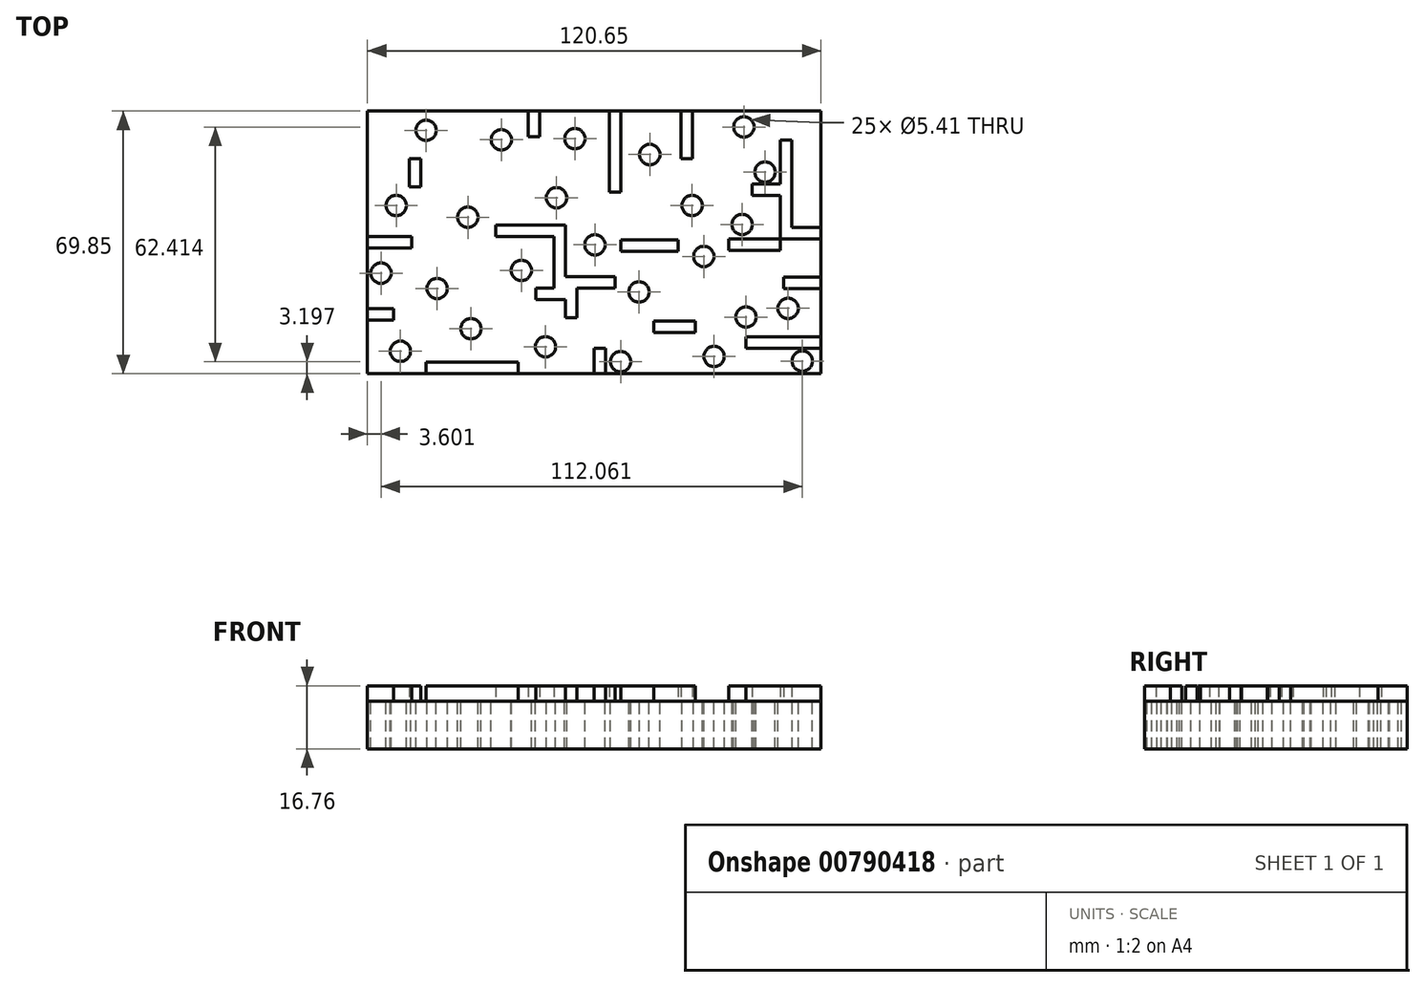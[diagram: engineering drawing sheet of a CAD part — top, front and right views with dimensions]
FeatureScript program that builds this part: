
annotation { "Feature Type Name" : "Feature", "Feature Type Description" : "" }
export const myFeature = defineFeature(function(context is Context, id is Id, definition is map)
    precondition{}
    {
        {
            var Q0;
            Q0=qCreatedBy(makeId("Top.planeOp"),FACE);
            var sketch = newSketch(context, id + "F0", { "sketchPlane" : qUnion([Q0])});
            skLineSegment(sketch, "E0.bottom", {"start": v(-60.33, 0) * mm, "end": v(60.33, 0) * mm});
            skLineSegment(sketch, "E0.top", {"start": v(-60.32, -69.85) * mm, "end": v(60.33, -69.85) * mm});
            skLineSegment(sketch, "E0.left", {"start": v(-60.33, 0) * mm, "end": v(-60.32, -69.85) * mm});
            skLineSegment(sketch, "E0.right", {"start": v(60.33, 0) * mm, "end": v(60.33, -69.85) * mm});
            skLineSegment(sketch, "E1", {"start": v(-60.33, 0) * mm, "end": v(0, 0) * mm});
            skLineSegment(sketch, "E2", {"start": v(0, 0) * mm, "end": v(60.33, 0) * mm});
            skSolve(sketch);
        }
        {
            var Q0;
            Q0=makeQuery(id+"F0.imprint","IMPRINT",FACE,{"disambiguationData":[TD([[makeQuery(id+"F0.imprint","IMPRINT",EDGE,{"derivedFrom":sQuery(id+"F0.wireOp",EDGE,"E0.top")}),1.0]])]});
            extrude(context, id + "F1", {"entities" : qUnion([Q0]), "depth" : 12.7 * mm, "offsetDistance" : 25.4 * mm});
        }
        {
            var Q0;
            Q0=makeQuery(id+"F1.opExtrude","CAP_FACE",FACE,{"disambiguationData":[OSD([sQuery(id+"F0.wireOp",EDGE,"E0.top"),sQuery(id+"F0.wireOp",EDGE,"E0.left"),sQuery(id+"F0.wireOp",EDGE,"E0.right"),sQuery(id+"F0.wireOp",EDGE,"E1"),sQuery(id+"F0.wireOp",EDGE,"E2")])],"isStart":false});
            var sketch = newSketch(context, id + "F2", { "sketchPlane" : qUnion([Q0])});
            skCircle(sketch, "E3", {"center": v(39.81, -4.24) * mm, "radius": 2.7 * mm});
            skCircle(sketch, "E4", {"center": v(0.2, -35.6) * mm, "radius": 2.7 * mm});
            skCircle(sketch, "E5", {"center": v(40.37, -54.8) * mm, "radius": 2.7 * mm});
            skCircle(sketch, "E6", {"center": v(-52.68, -25.12) * mm, "radius": 2.7 * mm});
            skCircle(sketch, "E7", {"center": v(-5.14, -7.36) * mm, "radius": 2.7 * mm});
            skCircle(sketch, "E8", {"center": v(-56.72, -43.12) * mm, "radius": 2.7 * mm});
            skCircle(sketch, "E9", {"center": v(7.02, -66.65) * mm, "radius": 2.7 * mm});
            skCircle(sketch, "E10", {"center": v(-12.96, -62.7) * mm, "radius": 2.7 * mm});
            skCircle(sketch, "E11", {"center": v(-51.56, -63.9) * mm, "radius": 2.7 * mm});
            skCircle(sketch, "E12", {"center": v(-32.78, -57.9) * mm, "radius": 2.7 * mm});
            skCircle(sketch, "E13", {"center": v(14.78, -11.58) * mm, "radius": 2.7 * mm});
            skCircle(sketch, "E14", {"center": v(-41.78, -47.2) * mm, "radius": 2.7 * mm});
            skCircle(sketch, "E15", {"center": v(11.9, -48.12) * mm, "radius": 2.7 * mm});
            skCircle(sketch, "E16", {"center": v(55.34, -66.5) * mm, "radius": 2.7 * mm});
            skCircle(sketch, "E17", {"center": v(-10.03, -23.07) * mm, "radius": 2.7 * mm});
            skCircle(sketch, "E18", {"center": v(39.33, -30.19) * mm, "radius": 2.7 * mm});
            skCircle(sketch, "E19", {"center": v(-19.38, -42.39) * mm, "radius": 2.7 * mm});
            skCircle(sketch, "E20", {"center": v(31.87, -65.27) * mm, "radius": 2.7 * mm});
            skCircle(sketch, "E21", {"center": v(51.57, -52.49) * mm, "radius": 2.7 * mm});
            skCircle(sketch, "E22", {"center": v(29.14, -38.68) * mm, "radius": 2.7 * mm});
            skCircle(sketch, "E23", {"center": v(-33.62, -28.25) * mm, "radius": 2.7 * mm});
            skCircle(sketch, "E24", {"center": v(26.04, -25.12) * mm, "radius": 2.7 * mm});
            skCircle(sketch, "E25", {"center": v(-44.72, -5.13) * mm, "radius": 2.7 * mm});
            skCircle(sketch, "E26", {"center": v(-24.7, -7.65) * mm, "radius": 2.7 * mm});
            skCircle(sketch, "E27", {"center": v(45.44, -16.23) * mm, "radius": 2.7 * mm});
            skSolve(sketch);
        }
        {
            var Q0;
            Q0=makeQuery(id+"F2.imprint","IMPRINT",FACE,{"disambiguationData":[TD([[makeQuery(id+"F2.imprint","IMPRINT",EDGE,{"derivedFrom":sQuery(id+"F2.wireOp",EDGE,"E24")}),1.0]])]});
            var Q1;
            Q1=makeQuery(id+"F2.imprint","IMPRINT",FACE,{"disambiguationData":[TD([[makeQuery(id+"F2.imprint","IMPRINT",EDGE,{"derivedFrom":sQuery(id+"F2.wireOp",EDGE,"E18")}),1.0]])]});
            var Q2;
            Q2=makeQuery(id+"F2.imprint","IMPRINT",FACE,{"disambiguationData":[TD([[makeQuery(id+"F2.imprint","IMPRINT",EDGE,{"derivedFrom":sQuery(id+"F2.wireOp",EDGE,"to4Jlu8j-MwpS-2O0Z-pIMG-6wgfSFoDchnS")}),1.0]])]});
            var Q3;
            Q3=makeQuery(id+"F2.imprint","IMPRINT",FACE,{"disambiguationData":[TD([[makeQuery(id+"F2.imprint","IMPRINT",EDGE,{"derivedFrom":sQuery(id+"F2.wireOp",EDGE,"E21")}),1.0]])]});
            var Q4;
            Q4=makeQuery(id+"F2.imprint","IMPRINT",FACE,{"disambiguationData":[TD([[makeQuery(id+"F2.imprint","IMPRINT",EDGE,{"derivedFrom":sQuery(id+"F2.wireOp",EDGE,"E5")}),1.0]])]});
            var Q5;
            Q5=makeQuery(id+"F2.imprint","IMPRINT",FACE,{"disambiguationData":[TD([[makeQuery(id+"F2.imprint","IMPRINT",EDGE,{"derivedFrom":sQuery(id+"F2.wireOp",EDGE,"E22")}),1.0]])]});
            var Q6;
            Q6=makeQuery(id+"F2.imprint","IMPRINT",FACE,{"disambiguationData":[TD([[makeQuery(id+"F2.imprint","IMPRINT",EDGE,{"derivedFrom":sQuery(id+"F2.wireOp",EDGE,"E3")}),1.0]])]});
            var Q7;
            Q7=makeQuery(id+"F2.imprint","IMPRINT",FACE,{"disambiguationData":[TD([[makeQuery(id+"F2.imprint","IMPRINT",EDGE,{"derivedFrom":sQuery(id+"F2.wireOp",EDGE,"E13")}),1.0]])]});
            var Q8;
            Q8=makeQuery(id+"F2.imprint","IMPRINT",FACE,{"disambiguationData":[TD([[makeQuery(id+"F2.imprint","IMPRINT",EDGE,{"derivedFrom":sQuery(id+"F2.wireOp",EDGE,"E7")}),1.0]])]});
            var Q9;
            Q9=makeQuery(id+"F2.imprint","IMPRINT",FACE,{"disambiguationData":[TD([[makeQuery(id+"F2.imprint","IMPRINT",EDGE,{"derivedFrom":sQuery(id+"F2.wireOp",EDGE,"E17")}),1.0]])]});
            var Q10;
            Q10=makeQuery(id+"F2.imprint","IMPRINT",FACE,{"disambiguationData":[TD([[makeQuery(id+"F2.imprint","IMPRINT",EDGE,{"derivedFrom":sQuery(id+"F2.wireOp",EDGE,"E4")}),1.0]])]});
            var Q11;
            Q11=makeQuery(id+"F2.imprint","IMPRINT",FACE,{"disambiguationData":[TD([[makeQuery(id+"F2.imprint","IMPRINT",EDGE,{"derivedFrom":sQuery(id+"F2.wireOp",EDGE,"E15")}),1.0]])]});
            var Q12;
            Q12=makeQuery(id+"F2.imprint","IMPRINT",FACE,{"disambiguationData":[TD([[makeQuery(id+"F2.imprint","IMPRINT",EDGE,{"derivedFrom":sQuery(id+"F2.wireOp",EDGE,"E19")}),1.0]])]});
            var Q13;
            Q13=makeQuery(id+"F2.imprint","IMPRINT",FACE,{"disambiguationData":[TD([[makeQuery(id+"F2.imprint","IMPRINT",EDGE,{"derivedFrom":sQuery(id+"F2.wireOp",EDGE,"E26")}),1.0]])]});
            var Q14;
            Q14=makeQuery(id+"F2.imprint","IMPRINT",FACE,{"disambiguationData":[TD([[makeQuery(id+"F2.imprint","IMPRINT",EDGE,{"derivedFrom":sQuery(id+"F2.wireOp",EDGE,"E23")}),1.0]])]});
            var Q15;
            Q15=makeQuery(id+"F2.imprint","IMPRINT",FACE,{"disambiguationData":[TD([[makeQuery(id+"F2.imprint","IMPRINT",EDGE,{"derivedFrom":sQuery(id+"F2.wireOp",EDGE,"E12")}),1.0]])]});
            var Q16;
            Q16=makeQuery(id+"F2.imprint","IMPRINT",FACE,{"disambiguationData":[TD([[makeQuery(id+"F2.imprint","IMPRINT",EDGE,{"derivedFrom":sQuery(id+"F2.wireOp",EDGE,"E10")}),1.0]])]});
            var Q17;
            Q17=makeQuery(id+"F2.imprint","IMPRINT",FACE,{"disambiguationData":[TD([[makeQuery(id+"F2.imprint","IMPRINT",EDGE,{"derivedFrom":sQuery(id+"F2.wireOp",EDGE,"E9")}),1.0]])]});
            var Q18;
            Q18=makeQuery(id+"F2.imprint","IMPRINT",FACE,{"disambiguationData":[TD([[makeQuery(id+"F2.imprint","IMPRINT",EDGE,{"derivedFrom":sQuery(id+"F2.wireOp",EDGE,"E20")}),1.0]])]});
            var Q19;
            Q19=makeQuery(id+"F2.imprint","IMPRINT",FACE,{"disambiguationData":[TD([[makeQuery(id+"F2.imprint","IMPRINT",EDGE,{"derivedFrom":sQuery(id+"F2.wireOp",EDGE,"E16")}),1.0]])]});
            var Q20;
            Q20=makeQuery(id+"F2.imprint","IMPRINT",FACE,{"disambiguationData":[TD([[makeQuery(id+"F2.imprint","IMPRINT",EDGE,{"derivedFrom":sQuery(id+"F2.wireOp",EDGE,"E14")}),1.0]])]});
            var Q21;
            Q21=makeQuery(id+"F2.imprint","IMPRINT",FACE,{"disambiguationData":[TD([[makeQuery(id+"F2.imprint","IMPRINT",EDGE,{"derivedFrom":sQuery(id+"F2.wireOp",EDGE,"E8")}),1.0]])]});
            var Q22;
            Q22=makeQuery(id+"F2.imprint","IMPRINT",FACE,{"disambiguationData":[TD([[makeQuery(id+"F2.imprint","IMPRINT",EDGE,{"derivedFrom":sQuery(id+"F2.wireOp",EDGE,"E6")}),1.0]])]});
            var Q23;
            Q23=makeQuery(id+"F2.imprint","IMPRINT",FACE,{"disambiguationData":[TD([[makeQuery(id+"F2.imprint","IMPRINT",EDGE,{"derivedFrom":sQuery(id+"F2.wireOp",EDGE,"E25")}),1.0]])]});
            var Q24;
            Q24=makeQuery(id+"F2.imprint","IMPRINT",FACE,{"disambiguationData":[TD([[makeQuery(id+"F2.imprint","IMPRINT",EDGE,{"derivedFrom":sQuery(id+"F2.wireOp",EDGE,"E11")}),1.0]])]});
            extrude(context, id + "F3", {"entities" : qUnion([Q0, Q1, Q2, Q3, Q4, Q5, Q6, Q7, Q8, Q9, Q10, Q11, Q12, Q13, Q14, Q15, Q16, Q17, Q18, Q19, Q20, Q21, Q22, Q23, Q24]), "operationType" : NewBodyOperationType.REMOVE, "endBound" : BoundingType.THROUGH_ALL, "oppositeDirection" : true, "depth" : 25.4 * mm, "offsetDistance" : 25.4 * mm});
        }
        {
            var Q0;
            Q0=makeQuery(id+"F2.imprint","IMPRINT",FACE,{"disambiguationData":[TD([[makeQuery(id+"F2.imprint","IMPRINT",EDGE,{"derivedFrom":sQuery(id+"F2.wireOp",EDGE,"E27")}),1.0]])]});
            extrude(context, id + "F4", {"entities" : qUnion([Q0]), "operationType" : NewBodyOperationType.REMOVE, "endBound" : BoundingType.THROUGH_ALL, "oppositeDirection" : true, "depth" : 25.4 * mm, "offsetDistance" : 25.4 * mm});
        }
        {
            var Q0;
            Q0=makeQuery(id+"F1.opExtrude","CAP_FACE",FACE,{"disambiguationData":[OSD([sQuery(id+"F0.wireOp",EDGE,"E0.top"),sQuery(id+"F0.wireOp",EDGE,"E0.left"),sQuery(id+"F0.wireOp",EDGE,"E0.right"),sQuery(id+"F0.wireOp",EDGE,"E1"),sQuery(id+"F0.wireOp",EDGE,"E2")])],"isStart":false});
            var sketch = newSketch(context, id + "F5", { "sketchPlane" : qUnion([Q0])});
            skLineSegment(sketch, "E28.bottom", {"start": v(49.45, -7.7) * mm, "end": v(52.5, -7.7) * mm});
            skLineSegment(sketch, "E28.top", {"start": v(49.45, -31) * mm, "end": v(52.5, -31) * mm});
            skLineSegment(sketch, "E28.left", {"start": v(49.45, -7.7) * mm, "end": v(49.45, -31) * mm});
            skLineSegment(sketch, "E28.right", {"start": v(52.5, -7.7) * mm, "end": v(52.5, -31) * mm});
            skLineSegment(sketch, "E29.bottom", {"start": v(49.45, -31) * mm, "end": v(60.33, -31) * mm});
            skLineSegment(sketch, "E29.top", {"start": v(49.45, -34.04) * mm, "end": v(60.33, -34.04) * mm});
            skLineSegment(sketch, "E29.left", {"start": v(49.45, -31) * mm, "end": v(49.45, -34.04) * mm});
            skLineSegment(sketch, "E29.right", {"start": v(60.33, -31) * mm, "end": v(60.33, -34.04) * mm});
            skLineSegment(sketch, "E30.bottom", {"start": v(49.45, -19.35) * mm, "end": v(42, -19.35) * mm});
            skLineSegment(sketch, "E30.top", {"start": v(49.45, -22.4) * mm, "end": v(42, -22.4) * mm});
            skLineSegment(sketch, "E30.left", {"start": v(49.45, -19.35) * mm, "end": v(49.45, -22.4) * mm});
            skLineSegment(sketch, "E30.right", {"start": v(42, -19.35) * mm, "end": v(42, -22.4) * mm});
            skLineSegment(sketch, "E31.bottom", {"start": v(23.09, 0) * mm, "end": v(26.14, 0) * mm});
            skLineSegment(sketch, "E31.top", {"start": v(23.09, -12.73) * mm, "end": v(26.14, -12.73) * mm});
            skLineSegment(sketch, "E31.left", {"start": v(23.09, 0) * mm, "end": v(23.09, -12.73) * mm});
            skLineSegment(sketch, "E31.right", {"start": v(26.14, 0) * mm, "end": v(26.14, -12.73) * mm});
            skLineSegment(sketch, "E32.bottom", {"start": v(3.97, 0) * mm, "end": v(7.01, 0) * mm});
            skLineSegment(sketch, "E32.top", {"start": v(3.97, -21.6) * mm, "end": v(7.01, -21.6) * mm});
            skLineSegment(sketch, "E32.left", {"start": v(3.97, 0) * mm, "end": v(3.97, -21.6) * mm});
            skLineSegment(sketch, "E32.right", {"start": v(7.01, 0) * mm, "end": v(7.01, -21.6) * mm});
            skLineSegment(sketch, "E33.bottom", {"start": v(7.01, -34.24) * mm, "end": v(22.31, -34.24) * mm});
            skLineSegment(sketch, "E33.top", {"start": v(7.01, -37.3) * mm, "end": v(22.31, -37.3) * mm});
            skLineSegment(sketch, "E33.left", {"start": v(7.01, -34.24) * mm, "end": v(7.01, -37.3) * mm});
            skLineSegment(sketch, "E33.right", {"start": v(22.31, -34.24) * mm, "end": v(22.31, -37.3) * mm});
            skLineSegment(sketch, "E34.bottom", {"start": v(-10.73, -30.39) * mm, "end": v(-7.68, -30.39) * mm});
            skLineSegment(sketch, "E34.top", {"start": v(-10.73, -47.12) * mm, "end": v(-7.68, -47.12) * mm});
            skLineSegment(sketch, "E34.left", {"start": v(-10.73, -30.39) * mm, "end": v(-10.73, -47.12) * mm});
            skLineSegment(sketch, "E34.right", {"start": v(-7.68, -30.39) * mm, "end": v(-7.68, -47.12) * mm});
            skLineSegment(sketch, "E35.bottom", {"start": v(-17.57, 0) * mm, "end": v(-14.52, 0) * mm});
            skLineSegment(sketch, "E35.top", {"start": v(-17.57, -6.9) * mm, "end": v(-14.52, -6.9) * mm});
            skLineSegment(sketch, "E35.left", {"start": v(-17.57, 0) * mm, "end": v(-17.57, -6.9) * mm});
            skLineSegment(sketch, "E35.right", {"start": v(-14.52, 0) * mm, "end": v(-14.52, -6.9) * mm});
            skLineSegment(sketch, "E36.bottom", {"start": v(-10.73, -30.39) * mm, "end": v(-26.23, -30.39) * mm});
            skLineSegment(sketch, "E36.top", {"start": v(-10.73, -33.44) * mm, "end": v(-26.23, -33.44) * mm});
            skLineSegment(sketch, "E36.left", {"start": v(-10.73, -30.39) * mm, "end": v(-10.73, -33.44) * mm});
            skLineSegment(sketch, "E36.right", {"start": v(-26.23, -30.39) * mm, "end": v(-26.23, -33.44) * mm});
            skLineSegment(sketch, "E37.bottom", {"start": v(-48.57, -33.44) * mm, "end": v(-60.32, -33.44) * mm});
            skLineSegment(sketch, "E37.top", {"start": v(-48.57, -36.49) * mm, "end": v(-60.33, -36.49) * mm});
            skLineSegment(sketch, "E37.left", {"start": v(-48.57, -33.44) * mm, "end": v(-48.57, -36.49) * mm});
            skLineSegment(sketch, "E37.right", {"start": v(-60.33, -33.44) * mm, "end": v(-60.33, -36.49) * mm});
            skLineSegment(sketch, "E38.bottom", {"start": v(-49.17, -12.73) * mm, "end": v(-46.12, -12.73) * mm});
            skLineSegment(sketch, "E38.top", {"start": v(-49.17, -20.18) * mm, "end": v(-46.12, -20.18) * mm});
            skLineSegment(sketch, "E38.left", {"start": v(-49.17, -12.73) * mm, "end": v(-49.17, -20.18) * mm});
            skLineSegment(sketch, "E38.right", {"start": v(-46.12, -12.73) * mm, "end": v(-46.12, -20.18) * mm});
            skLineSegment(sketch, "E39.bottom", {"start": v(-44.74, -69.85) * mm, "end": v(-20.19, -69.85) * mm});
            skLineSegment(sketch, "E39.top", {"start": v(-44.74, -66.8) * mm, "end": v(-20.19, -66.8) * mm});
            skLineSegment(sketch, "E39.left", {"start": v(-44.74, -69.85) * mm, "end": v(-44.74, -66.8) * mm});
            skLineSegment(sketch, "E39.right", {"start": v(-20.19, -69.85) * mm, "end": v(-20.19, -66.8) * mm});
            skLineSegment(sketch, "E40.bottom", {"start": v(-60.32, -52.56) * mm, "end": v(-53.4, -52.56) * mm});
            skLineSegment(sketch, "E40.top", {"start": v(-60.32, -55.6) * mm, "end": v(-53.4, -55.6) * mm});
            skLineSegment(sketch, "E40.left", {"start": v(-60.32, -52.56) * mm, "end": v(-60.32, -55.6) * mm});
            skLineSegment(sketch, "E40.right", {"start": v(-53.4, -52.56) * mm, "end": v(-53.4, -55.6) * mm});
            skLineSegment(sketch, "E41.bottom", {"start": v(-7.68, -47.12) * mm, "end": v(-15.56, -47.12) * mm});
            skLineSegment(sketch, "E41.top", {"start": v(-7.68, -50.17) * mm, "end": v(-15.56, -50.17) * mm});
            skLineSegment(sketch, "E41.left", {"start": v(-7.68, -47.12) * mm, "end": v(-7.68, -50.17) * mm});
            skLineSegment(sketch, "E41.right", {"start": v(-15.56, -47.12) * mm, "end": v(-15.56, -50.17) * mm});
            skLineSegment(sketch, "E42.bottom", {"start": v(-7.68, -47.12) * mm, "end": v(-4.63, -47.12) * mm});
            skLineSegment(sketch, "E42.top", {"start": v(-7.68, -54.95) * mm, "end": v(-4.63, -54.95) * mm});
            skLineSegment(sketch, "E42.left", {"start": v(-7.68, -47.12) * mm, "end": v(-7.68, -54.95) * mm});
            skLineSegment(sketch, "E42.right", {"start": v(-4.63, -47.12) * mm, "end": v(-4.63, -54.95) * mm});
            skLineSegment(sketch, "E43.bottom", {"start": v(0, -69.85) * mm, "end": v(3.05, -69.85) * mm});
            skLineSegment(sketch, "E43.top", {"start": v(0, -63.05) * mm, "end": v(3.05, -63.05) * mm});
            skLineSegment(sketch, "E43.left", {"start": v(0, -69.85) * mm, "end": v(0, -63.05) * mm});
            skLineSegment(sketch, "E43.right", {"start": v(3.05, -69.85) * mm, "end": v(3.05, -63.05) * mm});
            skLineSegment(sketch, "E44.bottom", {"start": v(-7.68, -47.12) * mm, "end": v(5.58, -47.12) * mm});
            skLineSegment(sketch, "E44.top", {"start": v(-7.68, -44.08) * mm, "end": v(5.58, -44.08) * mm});
            skLineSegment(sketch, "E44.left", {"start": v(-7.68, -47.12) * mm, "end": v(-7.68, -44.08) * mm});
            skLineSegment(sketch, "E44.right", {"start": v(5.58, -47.12) * mm, "end": v(5.58, -44.08) * mm});
            skLineSegment(sketch, "E45.bottom", {"start": v(49.45, -34.04) * mm, "end": v(35.77, -34.04) * mm});
            skLineSegment(sketch, "E45.top", {"start": v(49.45, -37.09) * mm, "end": v(35.77, -37.09) * mm});
            skLineSegment(sketch, "E45.left", {"start": v(49.45, -34.04) * mm, "end": v(49.45, -37.09) * mm});
            skLineSegment(sketch, "E45.right", {"start": v(35.77, -34.04) * mm, "end": v(35.77, -37.09) * mm});
            skLineSegment(sketch, "E46.bottom", {"start": v(60.33, -60) * mm, "end": v(40.4, -60) * mm});
            skLineSegment(sketch, "E46.top", {"start": v(60.33, -63.05) * mm, "end": v(40.4, -63.05) * mm});
            skLineSegment(sketch, "E46.left", {"start": v(60.33, -60) * mm, "end": v(60.33, -63.05) * mm});
            skLineSegment(sketch, "E46.right", {"start": v(40.4, -60) * mm, "end": v(40.4, -63.05) * mm});
            skLineSegment(sketch, "E47.bottom", {"start": v(15.84, -55.9) * mm, "end": v(26.91, -55.9) * mm});
            skLineSegment(sketch, "E47.top", {"start": v(15.84, -58.94) * mm, "end": v(26.91, -58.94) * mm});
            skLineSegment(sketch, "E47.left", {"start": v(15.84, -55.9) * mm, "end": v(15.84, -58.94) * mm});
            skLineSegment(sketch, "E47.right", {"start": v(26.91, -55.9) * mm, "end": v(26.91, -58.94) * mm});
            skLineSegment(sketch, "E48.bottom", {"start": v(60.33, -44.2) * mm, "end": v(50.34, -44.2) * mm});
            skLineSegment(sketch, "E48.top", {"start": v(60.33, -47.25) * mm, "end": v(50.34, -47.25) * mm});
            skLineSegment(sketch, "E48.left", {"start": v(60.33, -44.2) * mm, "end": v(60.33, -47.25) * mm});
            skLineSegment(sketch, "E48.right", {"start": v(50.34, -44.2) * mm, "end": v(50.34, -47.25) * mm});
            skPoint(sketch, "E49", {"position": v(51, -20.87) * mm});
            skPoint(sketch, "E49.positionSnap0", {"position": v(42, -20.87) * mm});
            skPoint(sketch, "E50", {"position": v(42.6, -35.57) * mm});
            skPoint(sketch, "E50.positionSnap0", {"position": v(42.6, -34.04) * mm});
            skPoint(sketch, "E50.positionSnap1", {"position": v(49.45, -35.57) * mm});
            skPoint(sketch, "E51", {"position": v(24.61, -6.37) * mm});
            skPoint(sketch, "E51.positionSnap0", {"position": v(24.61, -12.73) * mm});
            skPoint(sketch, "E51.positionSnap1", {"position": v(26.14, -6.37) * mm});
            skPoint(sketch, "E52", {"position": v(1.52, -66.45) * mm});
            skPoint(sketch, "E52.positionSnap0", {"position": v(1.52, -69.85) * mm});
            skPoint(sketch, "E52.positionSnap1", {"position": v(0, -66.45) * mm});
            skPoint(sketch, "E53", {"position": v(21.38, -57.42) * mm});
            skPoint(sketch, "E53.positionSnap0", {"position": v(21.38, -55.9) * mm});
            skPoint(sketch, "E53.positionSnap1", {"position": v(15.84, -57.42) * mm});
            skSolve(sketch);
        }
        {
            var Q0;
            {var subQ5=sQuery(id+"F5.wireOp",EDGE,"E28.bottom");Q0=makeQuery(id+"F5.imprint","IMPRINT",FACE,{"disambiguationData":[TD([[makeQuery(id+"F5.imprint","IMPRINT",EDGE,{"derivedFrom":subQ5}),-1.0]])]});}
            var Q1;
            Q1=makeQuery(id+"F5.imprint","IMPRINT",FACE,{"disambiguationData":[TD([[makeQuery(id+"F5.imprint","IMPRINT",EDGE,{"derivedFrom":sQuery(id+"F5.wireOp",EDGE,"E30.bottom")}),1.0]])]});
            var Q2;
            Q2=makeQuery(id+"F5.imprint","IMPRINT",FACE,{"disambiguationData":[TD([[makeQuery(id+"F5.imprint","IMPRINT",EDGE,{"derivedFrom":sQuery(id+"F5.wireOp",EDGE,"E29.top")}),1.0]])]});
            var Q3;
            Q3=makeQuery(id+"F5.imprint","IMPRINT",FACE,{"disambiguationData":[TD([[makeQuery(id+"F5.imprint","IMPRINT",EDGE,{"derivedFrom":sQuery(id+"F5.wireOp",EDGE,"E45.bottom")}),1.0]])]});
            var Q4;
            Q4=makeQuery(id+"F5.imprint","IMPRINT",FACE,{"disambiguationData":[TD([[makeQuery(id+"F5.imprint","IMPRINT",EDGE,{"derivedFrom":sQuery(id+"F5.wireOp",EDGE,"E48.bottom")}),1.0]])]});
            var Q5;
            Q5=makeQuery(id+"F5.imprint","IMPRINT",FACE,{"disambiguationData":[TD([[makeQuery(id+"F5.imprint","IMPRINT",EDGE,{"derivedFrom":sQuery(id+"F5.wireOp",EDGE,"E46.bottom")}),1.0]])]});
            var Q6;
            Q6=makeQuery(id+"F5.imprint","IMPRINT",FACE,{"disambiguationData":[TD([[makeQuery(id+"F5.imprint","IMPRINT",EDGE,{"derivedFrom":sQuery(id+"F5.wireOp",EDGE,"E47.bottom")}),-1.0]])]});
            var Q7;
            Q7=makeQuery(id+"F5.imprint","IMPRINT",FACE,{"disambiguationData":[TD([[makeQuery(id+"F5.imprint","IMPRINT",EDGE,{"derivedFrom":sQuery(id+"F5.wireOp",EDGE,"E43.bottom")}),1.0]])]});
            var Q8;
            {var subQ3=sQuery(id+"F5.wireOp",EDGE,"E42.top");Q8=makeQuery(id+"F5.imprint","IMPRINT",FACE,{"disambiguationData":[TD([[makeQuery(id+"F5.imprint","IMPRINT",EDGE,{"derivedFrom":subQ3}),1.0]])]});}
            var Q9;
            {var subQ1=sQuery(id+"F5.wireOp",EDGE,"E41.top");Q9=makeQuery(id+"F5.imprint","IMPRINT",FACE,{"disambiguationData":[TD([[makeQuery(id+"F5.imprint","IMPRINT",EDGE,{"derivedFrom":subQ1}),-1.0]])]});}
            var Q10;
            Q10=makeQuery(id+"F5.imprint","IMPRINT",FACE,{"disambiguationData":[TD([[makeQuery(id+"F5.imprint","IMPRINT",EDGE,{"derivedFrom":sQuery(id+"F5.wireOp",EDGE,"E34.bottom")}),-1.0]])]});
            var Q11;
            Q11=makeQuery(id+"F5.imprint","IMPRINT",FACE,{"disambiguationData":[TD([[makeQuery(id+"F5.imprint","IMPRINT",EDGE,{"derivedFrom":sQuery(id+"F5.wireOp",EDGE,"E44.top")}),-1.0]])]});
            var Q12;
            Q12=makeQuery(id+"F5.imprint","IMPRINT",FACE,{"disambiguationData":[TD([[makeQuery(id+"F5.imprint","IMPRINT",EDGE,{"derivedFrom":sQuery(id+"F5.wireOp",EDGE,"E36.bottom")}),1.0]])]});
            var Q13;
            Q13=makeQuery(id+"F5.imprint","IMPRINT",FACE,{"disambiguationData":[TD([[makeQuery(id+"F5.imprint","IMPRINT",EDGE,{"derivedFrom":sQuery(id+"F5.wireOp",EDGE,"E38.bottom")}),-1.0]])]});
            var Q14;
            Q14=makeQuery(id+"F5.imprint","IMPRINT",FACE,{"disambiguationData":[TD([[makeQuery(id+"F5.imprint","IMPRINT",EDGE,{"derivedFrom":sQuery(id+"F5.wireOp",EDGE,"E35.bottom")}),-1.0]])]});
            var Q15;
            Q15=makeQuery(id+"F5.imprint","IMPRINT",FACE,{"disambiguationData":[TD([[makeQuery(id+"F5.imprint","IMPRINT",EDGE,{"derivedFrom":sQuery(id+"F5.wireOp",EDGE,"E32.bottom")}),-1.0]])]});
            var Q16;
            Q16=makeQuery(id+"F5.imprint","IMPRINT",FACE,{"disambiguationData":[TD([[makeQuery(id+"F5.imprint","IMPRINT",EDGE,{"derivedFrom":sQuery(id+"F5.wireOp",EDGE,"E31.bottom")}),-1.0]])]});
            var Q17;
            Q17=makeQuery(id+"F5.imprint","IMPRINT",FACE,{"disambiguationData":[TD([[makeQuery(id+"F5.imprint","IMPRINT",EDGE,{"derivedFrom":sQuery(id+"F5.wireOp",EDGE,"E33.bottom")}),-1.0]])]});
            var Q18;
            Q18=makeQuery(id+"F5.imprint","IMPRINT",FACE,{"disambiguationData":[TD([[makeQuery(id+"F5.imprint","IMPRINT",EDGE,{"derivedFrom":sQuery(id+"F5.wireOp",EDGE,"E39.bottom")}),1.0]])]});
            var Q19;
            Q19=makeQuery(id+"F5.imprint","IMPRINT",FACE,{"disambiguationData":[TD([[makeQuery(id+"F5.imprint","IMPRINT",EDGE,{"derivedFrom":sQuery(id+"F5.wireOp",EDGE,"E40.bottom")}),-1.0]])]});
            var Q20;
            Q20=makeQuery(id+"F5.imprint","IMPRINT",FACE,{"disambiguationData":[TD([[makeQuery(id+"F5.imprint","IMPRINT",EDGE,{"derivedFrom":sQuery(id+"F5.wireOp",EDGE,"E37.bottom")}),1.0]])]});
            extrude(context, id + "F6", {"entities" : qUnion([Q0, Q1, Q2, Q3, Q4, Q5, Q6, Q7, Q8, Q9, Q10, Q11, Q12, Q13, Q14, Q15, Q16, Q17, Q18, Q19, Q20]), "depth" : 4.06 * mm, "offsetDistance" : 25.4 * mm});
        }
    });
